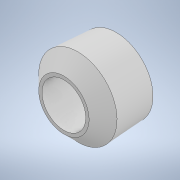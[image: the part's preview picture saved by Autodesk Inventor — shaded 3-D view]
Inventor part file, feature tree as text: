
AUTODESK INVENTOR PART (.ipt)
format: ipt  version: 2022 (Build 260153000, 153)  size: 115,200 bytes
history: native  units: mm
features: revolve x1, sketch x1
ambient origin geometry x8: Origin, YZ Plane, XZ Plane, XY Plane, X Axis, Y Axis, Z Axis, Center Point
bodies: Volumenkörper1 (feature_tree)
feature tree (2):
  revolve  "Umdrehung1"
  sketch  "Skizze1"  dims[d0=3.35mm d1=5.65mm d2=6.0mm d3=8.0mm d4=45.0deg d5=90.0deg]
